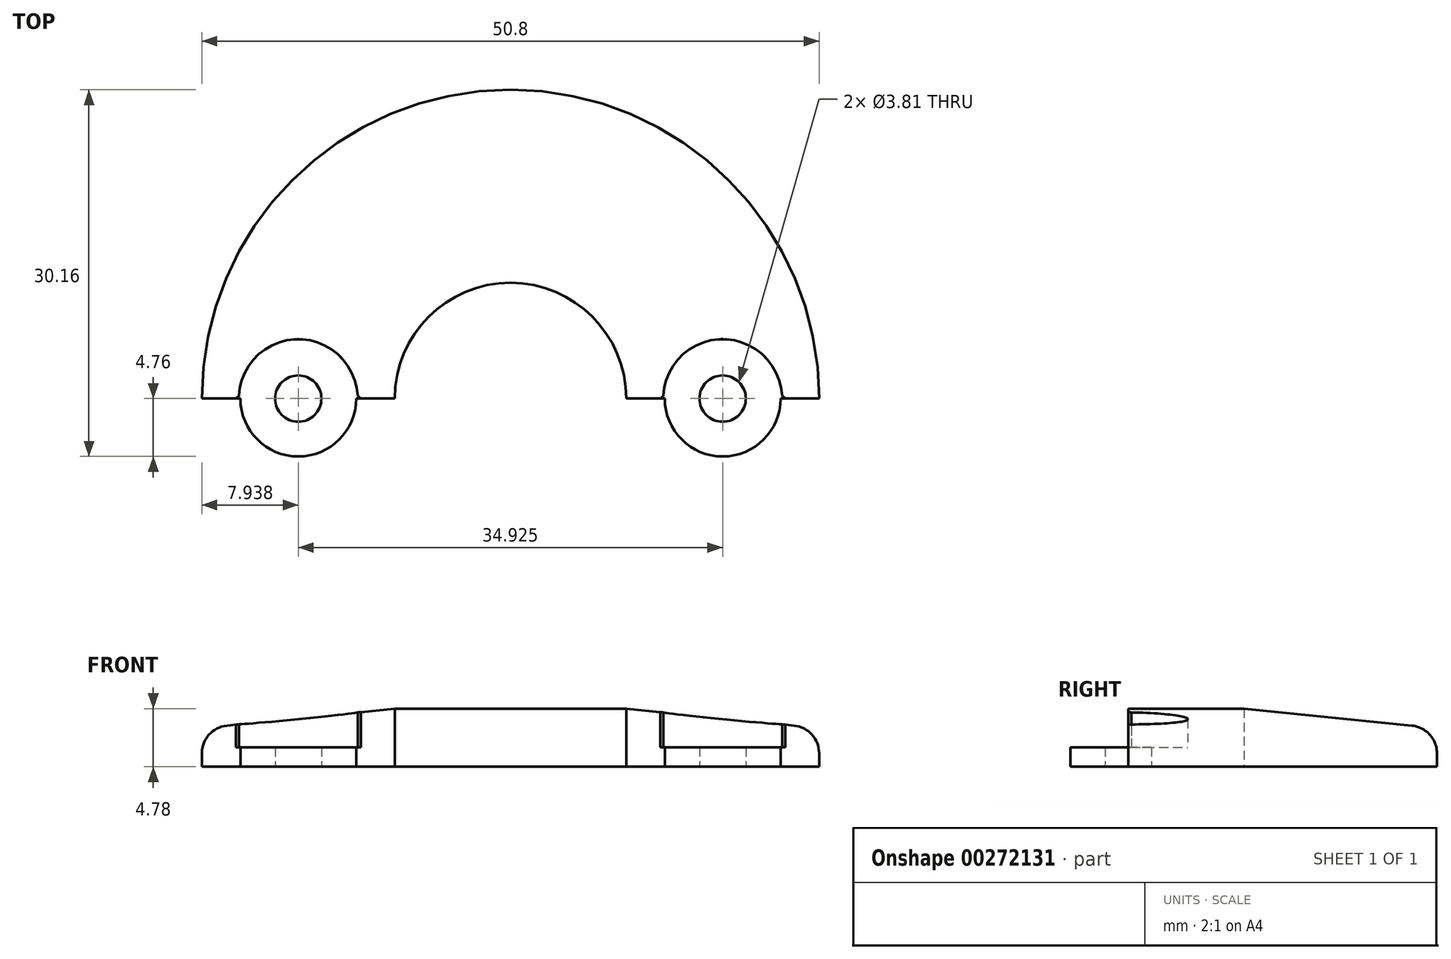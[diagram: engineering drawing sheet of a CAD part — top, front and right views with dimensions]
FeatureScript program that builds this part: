
annotation { "Feature Type Name" : "Feature", "Feature Type Description" : "" }
export const myFeature = defineFeature(function(context is Context, id is Id, definition is map)
    precondition{}
    {
        {
            var Q0;
            Q0=qCreatedBy(makeId("Front.planeOp"),FACE);
            var sketch = newSketch(context, id + "F0", { "sketchPlane" : qUnion([Q0])});
            skLineSegment(sketch, "E0", {"start": v(9.53, 0) * mm, "end": v(25.4, 0) * mm});
            skLineSegment(sketch, "E1", {"start": v(25.4, 0) * mm, "end": v(25.4, 1.1) * mm});
            skLineSegment(sketch, "E2", {"start": v(23.34, 3.38) * mm, "end": v(9.52, 4.78) * mm});
            skLineSegment(sketch, "E3", {"start": v(9.53, 4.78) * mm, "end": v(9.53, 0) * mm});
            skPoint(sketch, "E4.visualSharp", {"position": v(25.4, 3.18) * mm});
            skArc(sketch, "E4.filletArc", {"start": v(25.4, 1.1) * mm, "mid": v(24.8, 2.64) * mm, "end": v(23.34, 3.38) * mm});
            skLineSegment(sketch, "E5", {"start": v(0, 0) * mm, "end": v(0, 4.4) * mm});
            skSolve(sketch);
        }
        {
            var Q0;
            Q0=makeQuery(id+"F0.imprint","IMPRINT",FACE,{"disambiguationData":[TD([[makeQuery(id+"F0.imprint","IMPRINT",EDGE,{"derivedFrom":sQuery(id+"F0.wireOp",EDGE,"E0")}),1.0]])]});
            var Q1;
            Q1=sQuery(id+"F0.wireOp",EDGE,"E5");
            revolve(context, id + "F1", {"entities" : qUnion([Q0]), "axis" : qUnion([Q1]), "revolveType" : RevolveType.FULL});
        }
        {
            var Q0;
            Q0=makeQuery(id+"F1.opRevolve","SWEPT_FACE",FACE,{"disambiguationData":[OSD([sQuery(id+"F0.wireOp",EDGE,"E0")])]});
            var sketch = newSketch(context, id + "F2", { "sketchPlane" : qUnion([Q0])});
            skLineSegment(sketch, "E6.bottom", {"start": v(-25.4, 0) * mm, "end": v(25.4, 0) * mm});
            skLineSegment(sketch, "E6.top", {"start": v(-25.4, 25.4) * mm, "end": v(25.4, 25.4) * mm});
            skLineSegment(sketch, "E6.left", {"start": v(-25.4, 0) * mm, "end": v(-25.4, 25.4) * mm});
            skLineSegment(sketch, "E6.right", {"start": v(25.4, 0) * mm, "end": v(25.4, 25.4) * mm});
            skSolve(sketch);
        }
        {
            var Q0;
            Q0 = qSketchRegion(id + "F2", true);
            extrude(context, id + "F3", {"entities" : qUnion([Q0]), "operationType" : NewBodyOperationType.REMOVE, "endBound" : BoundingType.THROUGH_ALL, "oppositeDirection" : true, "depth" : 25.4 * mm});
        }
        {
            var Q0;
            Q0=makeQuery(id+"F1.opRevolve","SWEPT_FACE",FACE,{"disambiguationData":[OSD([sQuery(id+"F0.wireOp",EDGE,"E0")])]});
            var sketch = newSketch(context, id + "F4", { "sketchPlane" : qUnion([Q0])});
            skCircle(sketch, "E7", {"center": v(-17.46, 0) * mm, "radius": 4.76 * mm});
            skCircle(sketch, "E8", {"center": v(17.46, 0) * mm, "radius": 4.76 * mm});
            skSolve(sketch);
        }
        {
            var Q0;
            Q0 = qSketchRegion(id + "F4", true);
            extrude(context, id + "F5", {"entities" : qUnion([Q0]), "operationType" : NewBodyOperationType.ADD, "oppositeDirection" : true, "depth" : 1.6 * mm});
        }
        {
            var Q0;
            Q0=makeQuery(id+"F5.opExtrude","CAP_FACE",FACE,{"disambiguationData":[OSD([sQuery(id+"F4.wireOp",EDGE,"E7")])],"isStart":false});
            var sketch = newSketch(context, id + "F6", { "sketchPlane" : qUnion([Q0])});
            skCircle(sketch, "E9", {"center": v(-17.46, 0) * mm, "radius": 4.89 * mm});
            skCircle(sketch, "E10", {"center": v(17.46, 0) * mm, "radius": 4.89 * mm});
            skSolve(sketch);
        }
        {
            var Q0;
            Q0 = qSketchRegion(id + "F6", true);
            extrude(context, id + "F7", {"entities" : qUnion([Q0]), "operationType" : NewBodyOperationType.REMOVE, "endBound" : BoundingType.THROUGH_ALL, "depth" : 25.4 * mm});
        }
        {
            var Q0;
            Q0=makeQuery(id+"F5.boolean.opBoolean","MERGE",FACE,{"derivedFrom":[makeQuery(id+"F1.opRevolve","SWEPT_FACE",FACE,{"disambiguationData":[OSD([sQuery(id+"F0.wireOp",EDGE,"E0")])]}),makeQuery(id+"F5.opExtrude","CAP_FACE",FACE,{"disambiguationData":[OSD([sQuery(id+"F4.wireOp",EDGE,"E7")])],"isStart":true}),makeQuery(id+"F5.opExtrude","CAP_FACE",FACE,{"disambiguationData":[OSD([sQuery(id+"F4.wireOp",EDGE,"E8")])],"isStart":true})]});
            var sketch = newSketch(context, id + "F8", { "sketchPlane" : qUnion([Q0])});
            skCircle(sketch, "E11", {"center": v(-17.46, 0) * mm, "radius": 1.9 * mm});
            skCircle(sketch, "E12", {"center": v(17.46, 0) * mm, "radius": 1.9 * mm});
            skSolve(sketch);
        }
        {
            var Q0;
            Q0 = qSketchRegion(id + "F8", true);
            extrude(context, id + "F9", {"entities" : qUnion([Q0]), "operationType" : NewBodyOperationType.REMOVE, "endBound" : BoundingType.THROUGH_ALL, "oppositeDirection" : true, "depth" : 25.4 * mm});
        }
        {
            var Q0;
            Q0=makeQuery(id+"F7.boolean.opBoolean","INTERSECT",EDGE,{"disambiguationData":[OD(0.0)],"derivedFrom":[makeQuery(id+"F3.boolean.opBoolean","COPY",FACE,{"disambiguationData":[OD(0.0)],"derivedFrom":makeQuery(id+"F3.opExtrude","SWEPT_FACE",FACE,{"disambiguationData":[OSD([sQuery(id+"F2.wireOp",EDGE,"E6.bottom")])]})}),makeQuery(id+"F7.opExtrude","SWEPT_FACE",FACE,{"disambiguationData":[OSD([sQuery(id+"F6.wireOp",EDGE,"E9")])]})]});
            var Q1;
            Q1=makeQuery(id+"F7.boolean.opBoolean","INTERSECT",EDGE,{"disambiguationData":[OD(1.0)],"derivedFrom":[makeQuery(id+"F3.boolean.opBoolean","COPY",FACE,{"disambiguationData":[OD(0.0)],"derivedFrom":makeQuery(id+"F3.opExtrude","SWEPT_FACE",FACE,{"disambiguationData":[OSD([sQuery(id+"F2.wireOp",EDGE,"E6.bottom")])]})}),makeQuery(id+"F7.opExtrude","SWEPT_FACE",FACE,{"disambiguationData":[OSD([sQuery(id+"F6.wireOp",EDGE,"E9")])]})]});
            var Q2;
            Q2=makeQuery(id+"F7.boolean.opBoolean","INTERSECT",EDGE,{"disambiguationData":[OD(1.0)],"derivedFrom":[makeQuery(id+"F3.boolean.opBoolean","COPY",FACE,{"disambiguationData":[OD(1.0)],"derivedFrom":makeQuery(id+"F3.opExtrude","SWEPT_FACE",FACE,{"disambiguationData":[OSD([sQuery(id+"F2.wireOp",EDGE,"E6.bottom")])]})}),makeQuery(id+"F7.opExtrude","SWEPT_FACE",FACE,{"disambiguationData":[OSD([sQuery(id+"F6.wireOp",EDGE,"E10")])]})]});
            var Q3;
            Q3=makeQuery(id+"F7.boolean.opBoolean","INTERSECT",EDGE,{"disambiguationData":[OD(0.0)],"derivedFrom":[makeQuery(id+"F3.boolean.opBoolean","COPY",FACE,{"disambiguationData":[OD(1.0)],"derivedFrom":makeQuery(id+"F3.opExtrude","SWEPT_FACE",FACE,{"disambiguationData":[OSD([sQuery(id+"F2.wireOp",EDGE,"E6.bottom")])]})}),makeQuery(id+"F7.opExtrude","SWEPT_FACE",FACE,{"disambiguationData":[OSD([sQuery(id+"F6.wireOp",EDGE,"E10")])]})]});
            chamfer(context, id + "F10", {"entities" : qUnion([Q0, Q1, Q2, Q3]), "width" : 0.25 * mm, "tangentPropagation" : true});
        }
    });
